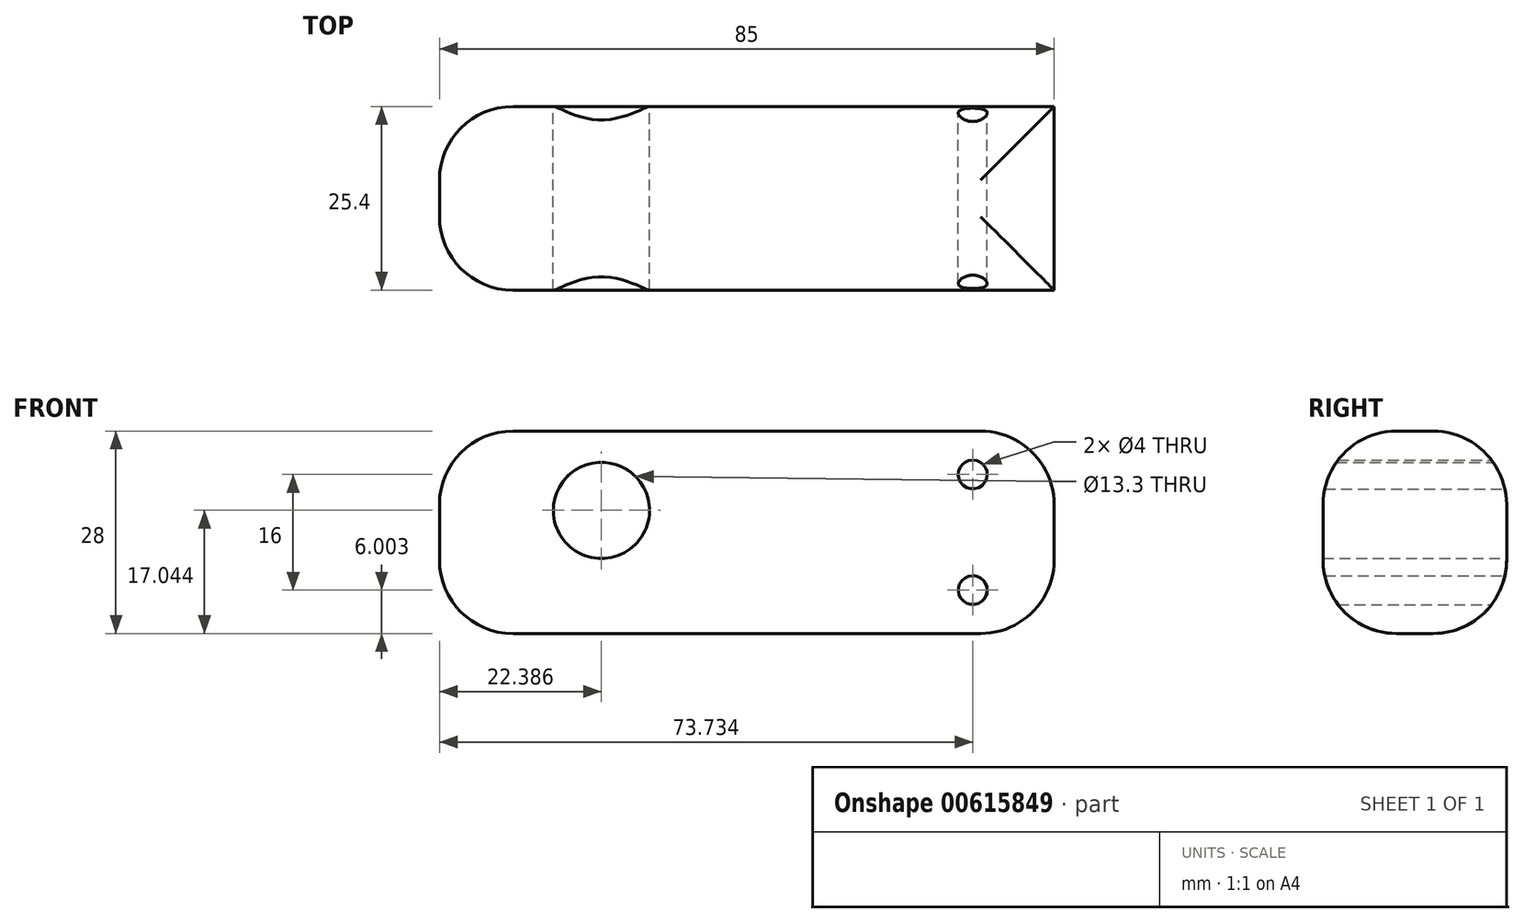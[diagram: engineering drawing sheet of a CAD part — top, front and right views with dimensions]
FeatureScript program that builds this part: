
annotation { "Feature Type Name" : "Feature", "Feature Type Description" : "" }
export const myFeature = defineFeature(function(context is Context, id is Id, definition is map)
    precondition{}
    {
        {
            var Q0;
            Q0=qCreatedBy(makeId("Front.planeOp"),FACE);
            var sketch = newSketch(context, id + "F0", { "sketchPlane" : qUnion([Q0])});
            skLineSegment(sketch, "E0.bottom", {"start": v(-66.23, -17.49) * mm, "end": v(18.77, -17.49) * mm});
            skLineSegment(sketch, "E0.top", {"start": v(-66.23, -45.49) * mm, "end": v(18.77, -45.49) * mm});
            skLineSegment(sketch, "E0.left", {"start": v(-66.23, -17.49) * mm, "end": v(-66.23, -45.49) * mm});
            skLineSegment(sketch, "E0.right", {"start": v(18.77, -17.49) * mm, "end": v(18.77, -45.49) * mm});
            skSolve(sketch);
        }
        {
            var Q0;
            Q0 = qSketchRegion(id + "F0", true);
            extrude(context, id + "F1", {"entities" : qUnion([Q0]), "depth" : 25.4 * mm, "offsetDistance" : 25.4 * mm});
        }
        {
            var Q0;
            Q0=makeQuery(id+"F1.opExtrude","SWEPT_FACE",FACE,{"disambiguationData":[OSD([sQuery(id+"F0.wireOp",EDGE,"E0.left")])]});
            var Q1;
            Q1=makeQuery(id+"F1.opExtrude","SWEPT_FACE",FACE,{"disambiguationData":[OSD([sQuery(id+"F0.wireOp",EDGE,"E0.bottom")])]});
            var Q2;
            Q2=makeQuery(id+"F1.opExtrude","SWEPT_FACE",FACE,{"disambiguationData":[OSD([sQuery(id+"F0.wireOp",EDGE,"E0.top")])]});
            fillet(context, id + "F2", {"entities" : qUnion([Q0, Q1, Q2]), "radius" : 10.16 * mm, "tangentPropagation" : true, "allowEdgeOverflow" : false});
        }
        {
            var Q0;
            Q0=makeQuery(id+"F1.opExtrude","CAP_FACE",FACE,{"disambiguationData":[OSD([sQuery(id+"F0.wireOp",EDGE,"E0.bottom"),sQuery(id+"F0.wireOp",EDGE,"E0.top"),sQuery(id+"F0.wireOp",EDGE,"E0.left"),sQuery(id+"F0.wireOp",EDGE,"E0.right")])],"isStart":true});
            var sketch = newSketch(context, id + "F3", { "sketchPlane" : qUnion([Q0])});
            skCircle(sketch, "E1", {"center": v(43.84, -28.45) * mm, "radius": 6.65 * mm});
            skSolve(sketch);
        }
        {
            var Q0;
            Q0=makeQuery(id+"F3.imprint","IMPRINT",FACE,{"disambiguationData":[TD([[makeQuery(id+"F3.imprint","IMPRINT",EDGE,{"derivedFrom":sQuery(id+"F3.wireOp",EDGE,"E1")}),1.0]])]});
            extrude(context, id + "F4", {"entities" : qUnion([Q0]), "operationType" : NewBodyOperationType.REMOVE, "oppositeDirection" : true, "depth" : 25.4 * mm, "offsetDistance" : 25.4 * mm});
        }
        {
            var Q0;
            Q0=qCreatedBy(makeId("Front.planeOp"),FACE);
            var sketch = newSketch(context, id + "F5", { "sketchPlane" : qUnion([Q0])});
            skCircle(sketch, "E2", {"center": v(7.5, -23.49) * mm, "radius": 2 * mm});
            skCircle(sketch, "E3.0.1.0", {"center": v(7.5, -39.49) * mm, "radius": 2 * mm});
            skLineSegment(sketch, "E3.direction1", {"start": v(7.5, -23.49) * mm, "end": v(32.5, -23.49) * mm, "construction": true});
            skLineSegment(sketch, "E3.direction2", {"start": v(7.5, -23.49) * mm, "end": v(7.5, -39.49) * mm, "construction": true});
            skSolve(sketch);
        }
        {
            var Q0;
            Q0=qCreatedBy(makeId("Front.planeOp"),FACE);
            var sketch = newSketch(context, id + "F6", { "sketchPlane" : qUnion([Q0])});
            skCircle(sketch, "E4", {"center": v(7.88, -39.9) * mm, "radius": 2 * mm});
            skSolve(sketch);
        }
        {
            var Q0;
            Q0 = qSketchRegion(id + "F5", true);
            extrude(context, id + "F7", {"entities" : qUnion([Q0]), "operationType" : NewBodyOperationType.REMOVE, "depth" : 35 * mm, "offsetDistance" : 25 * mm});
        }
    });
